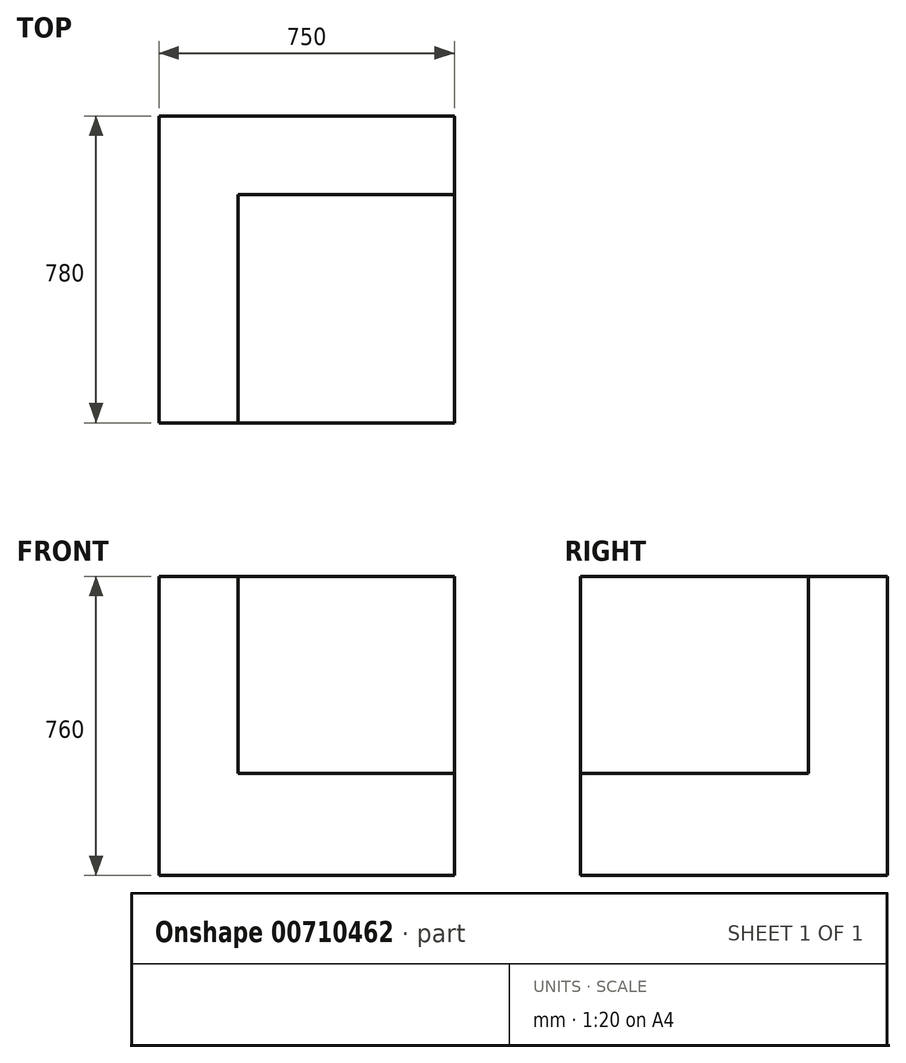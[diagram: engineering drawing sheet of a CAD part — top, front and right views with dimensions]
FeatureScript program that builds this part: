
annotation { "Feature Type Name" : "Feature", "Feature Type Description" : "" }
export const myFeature = defineFeature(function(context is Context, id is Id, definition is map)
    precondition{}
    {
        {
            var Q0;
            Q0=qCreatedBy(makeId("Top.planeOp"),FACE);
            var sketch = newSketch(context, id + "F0", { "sketchPlane" : qUnion([Q0])});
            skLineSegment(sketch, "E0.bottom", {"start": v(375, 390) * mm, "end": v(-375, 390) * mm});
            skLineSegment(sketch, "E0.top", {"start": v(375, -390) * mm, "end": v(-375, -390) * mm});
            skLineSegment(sketch, "E0.left", {"start": v(375, 390) * mm, "end": v(375, -390) * mm});
            skLineSegment(sketch, "E0.right", {"start": v(-375, 390) * mm, "end": v(-375, -390) * mm});
            skPoint(sketch, "E0.middle", {"position": v(0, 0) * mm});
            skSolve(sketch);
        }
        {
            var Q0;
            Q0=makeQuery(id+"F0.imprint","IMPRINT",FACE,{"disambiguationData":[TD([[makeQuery(id+"F0.imprint","IMPRINT",EDGE,{"derivedFrom":sQuery(id+"F0.wireOp",EDGE,"E0.bottom")}),1.0]])]});
            extrude(context, id + "F1", {"entities" : qUnion([Q0]), "depth" : 760 * mm, "offsetDistance" : 25 * mm});
        }
        {
            var Q0;
            Q0=makeQuery(id+"F1.opExtrude","CAP_FACE",FACE,{"disambiguationData":[OSD([sQuery(id+"F0.wireOp",EDGE,"E0.bottom"),sQuery(id+"F0.wireOp",EDGE,"E0.top"),sQuery(id+"F0.wireOp",EDGE,"E0.left"),sQuery(id+"F0.wireOp",EDGE,"E0.right")])],"isStart":false});
            var sketch = newSketch(context, id + "F2", { "sketchPlane" : qUnion([Q0])});
            skLineSegment(sketch, "E1.bottom", {"start": v(375, -390) * mm, "end": v(-175, -390) * mm});
            skLineSegment(sketch, "E1.top", {"start": v(375, 190) * mm, "end": v(-175, 190) * mm});
            skLineSegment(sketch, "E1.left", {"start": v(375, -390) * mm, "end": v(375, 190) * mm});
            skLineSegment(sketch, "E1.right", {"start": v(-175, -390) * mm, "end": v(-175, 190) * mm});
            skSolve(sketch);
        }
        {
            var Q0;
            Q0=makeQuery(id+"F2.imprint","IMPRINT",FACE,{"disambiguationData":[TD([[makeQuery(id+"F2.imprint","IMPRINT",EDGE,{"derivedFrom":sQuery(id+"F2.wireOp",EDGE,"E1.bottom")}),-1.0]])]});
            extrude(context, id + "F3", {"entities" : qUnion([Q0]), "operationType" : NewBodyOperationType.REMOVE, "oppositeDirection" : true, "depth" : 500 * mm, "offsetDistance" : 25 * mm});
        }
    });
